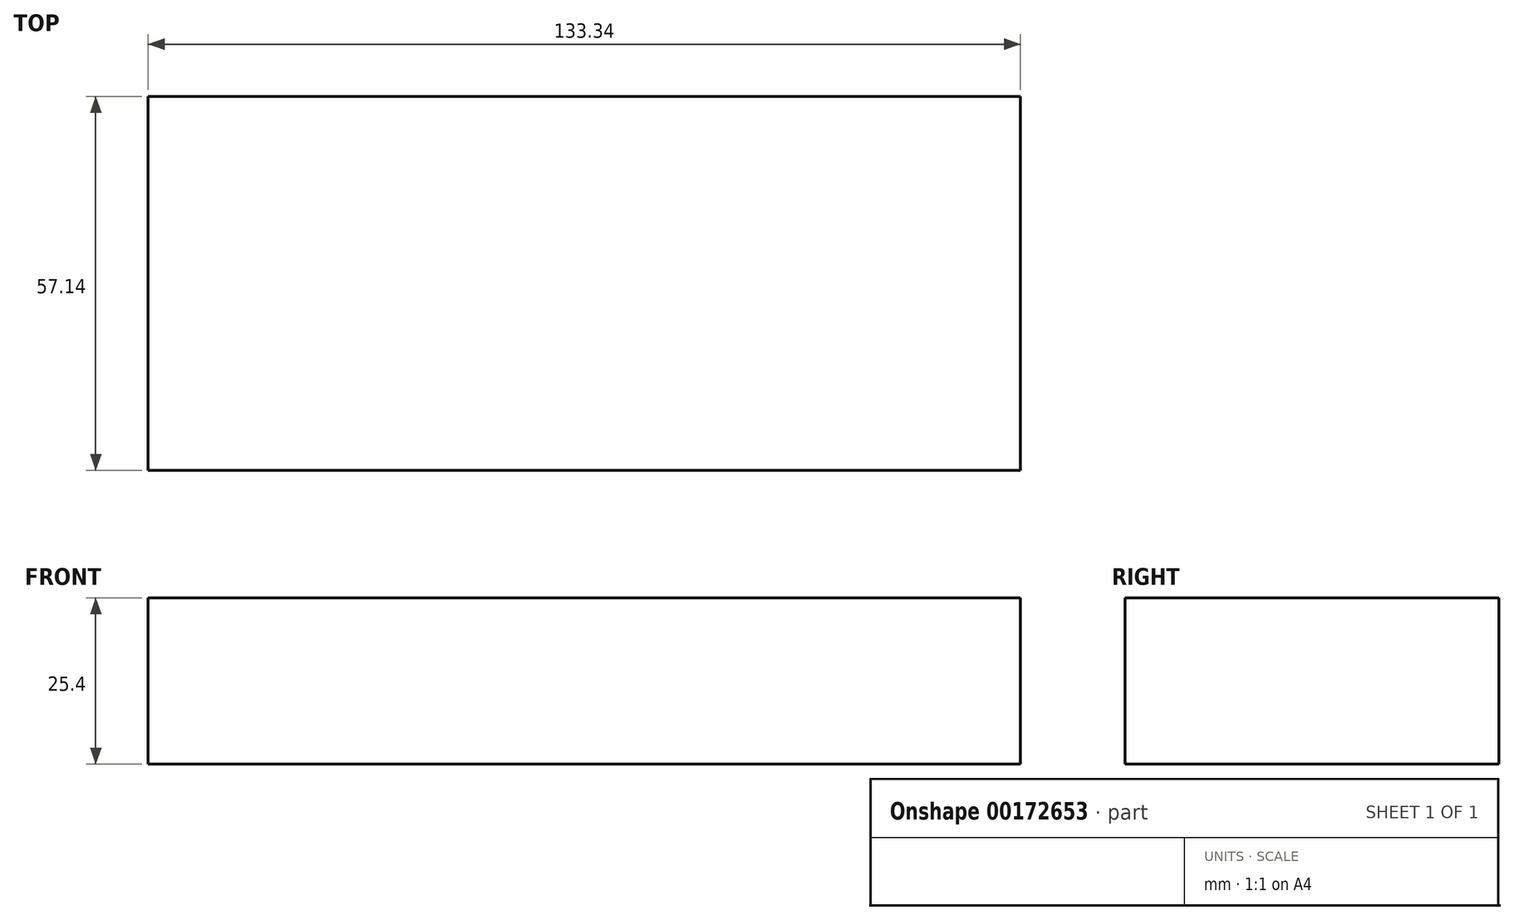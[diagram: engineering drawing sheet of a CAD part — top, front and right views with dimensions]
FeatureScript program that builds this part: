
annotation { "Feature Type Name" : "Feature", "Feature Type Description" : "" }
export const myFeature = defineFeature(function(context is Context, id is Id, definition is map)
    precondition{}
    {
        {
            var Q0;
            Q0=qCreatedBy(makeId("Top.planeOp"),FACE);
            var sketch = newSketch(context, id + "F0", { "sketchPlane" : qUnion([Q0])});
            skPoint(sketch, "E0.middle", {"position": v(0, 0) * mm});
            skLineSegment(sketch, "E1.bottom", {"start": v(66.68, 28.58) * mm, "end": v(-66.68, 28.58) * mm});
            skLineSegment(sketch, "E1.top", {"start": v(66.68, -28.57) * mm, "end": v(-66.68, -28.57) * mm});
            skLineSegment(sketch, "E1.left", {"start": v(66.68, 28.58) * mm, "end": v(66.68, -28.57) * mm});
            skLineSegment(sketch, "E1.right", {"start": v(-66.68, 28.58) * mm, "end": v(-66.68, -28.57) * mm});
            skSolve(sketch);
        }
        {
            var Q0;
            Q0=makeQuery(id+"F0.imprint","IMPRINT",FACE,{"disambiguationData":[TD([[makeQuery(id+"F0.imprint","IMPRINT",EDGE,{"derivedFrom":sQuery(id+"F0.wireOp",EDGE,"E1.bottom")}),1.0]])]});
            extrude(context, id + "F1", {"entities" : qUnion([Q0]), "depth" : 25.4 * mm});
        }
    });
